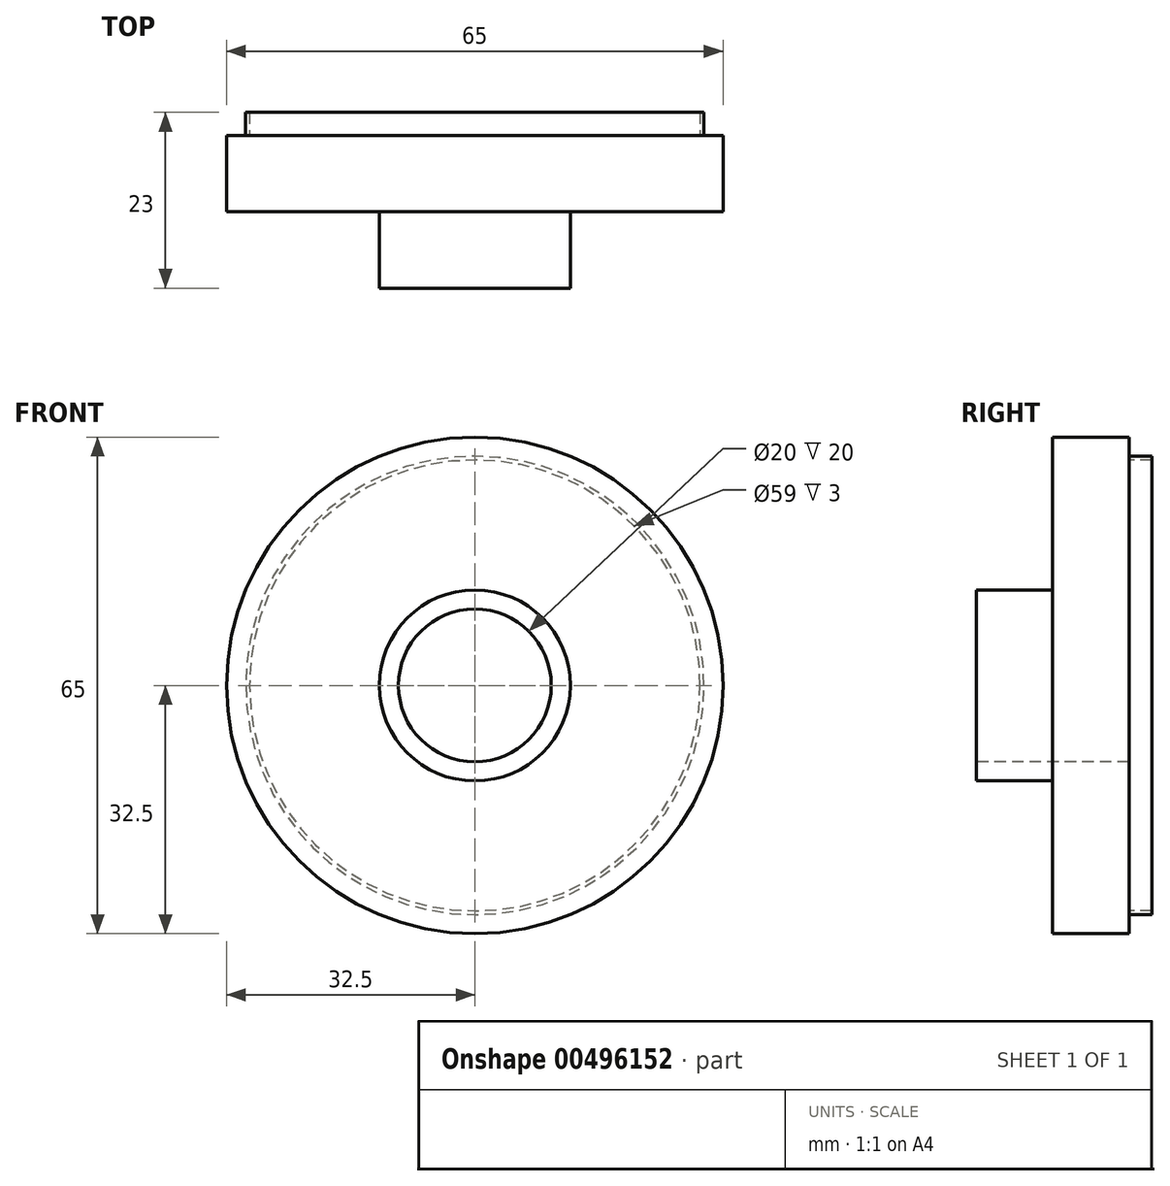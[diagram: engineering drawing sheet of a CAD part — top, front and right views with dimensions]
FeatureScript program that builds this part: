
annotation { "Feature Type Name" : "Feature", "Feature Type Description" : "" }
export const myFeature = defineFeature(function(context is Context, id is Id, definition is map)
    precondition{}
    {
        {
            var Q0;
            Q0=qCreatedBy(makeId("Front.planeOp"),FACE);
            var sketch = newSketch(context, id + "F0", { "sketchPlane" : qUnion([Q0])});
            skCircle(sketch, "E0", {"center": v(0, 0) * mm, "radius": 32.5 * mm});
            skSolve(sketch);
        }
        {
            var Q0;
            Q0 = qSketchRegion(id + "F0", true);
            extrude(context, id + "F1", {"entities" : qUnion([Q0]), "oppositeDirection" : true, "depth" : 10 * mm});
        }
        {
            var Q0;
            Q0=makeQuery(id+"F1.opExtrude","CAP_FACE",FACE,{"disambiguationData":[OSD([sQuery(id+"F0.wireOp",EDGE,"E0")])],"isStart":true});
            var sketch = newSketch(context, id + "F2", { "sketchPlane" : qUnion([Q0])});
            skCircle(sketch, "E1", {"center": v(0, 0) * mm, "radius": 12.5 * mm});
            skSolve(sketch);
        }
        {
            var Q0;
            Q0 = qSketchRegion(id + "F2", true);
            extrude(context, id + "F3", {"entities" : qUnion([Q0]), "operationType" : NewBodyOperationType.ADD, "depth" : 10 * mm});
        }
        {
            var Q0;
            Q0=makeQuery(id+"F3.opExtrude","CAP_FACE",FACE,{"disambiguationData":[OSD([sQuery(id+"F2.wireOp",EDGE,"E1")])],"isStart":false});
            var sketch = newSketch(context, id + "F4", { "sketchPlane" : qUnion([Q0])});
            skCircle(sketch, "E2", {"center": v(0, 0) * mm, "radius": 10 * mm});
            skSolve(sketch);
        }
        {
            var Q0;
            Q0 = qSketchRegion(id + "F4", true);
            extrude(context, id + "F5", {"entities" : qUnion([Q0]), "operationType" : NewBodyOperationType.REMOVE, "oppositeDirection" : true, "depth" : 20 * mm});
        }
        {
            var Q0;
            Q0=makeQuery(id+"F1.opExtrude","CAP_FACE",FACE,{"disambiguationData":[OSD([sQuery(id+"F0.wireOp",EDGE,"E0")])],"isStart":false});
            var sketch = newSketch(context, id + "F6", { "sketchPlane" : qUnion([Q0])});
            skCircle(sketch, "E3", {"center": v(0, 0) * mm, "radius": 30 * mm});
            skCircle(sketch, "E4", {"center": v(0, 0) * mm, "radius": 29.5 * mm});
            skSolve(sketch);
        }
        {
            var Q0;
            Q0 = qSketchRegion(id + "F6", true);
            extrude(context, id + "F7", {"entities" : qUnion([Q0]), "operationType" : NewBodyOperationType.ADD, "depth" : 3 * mm});
        }
    });
